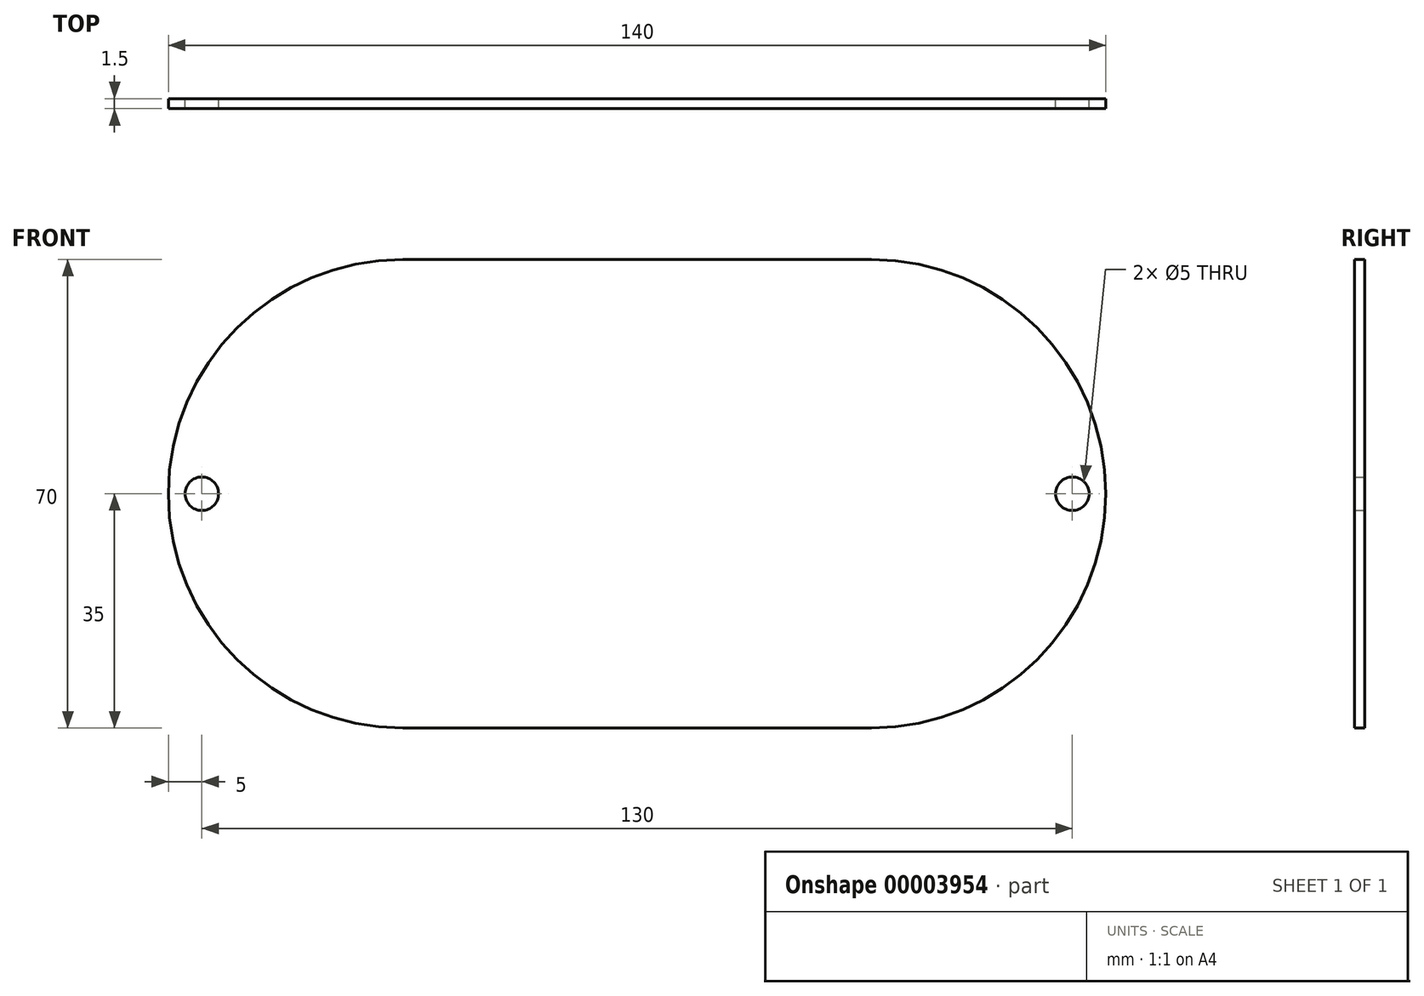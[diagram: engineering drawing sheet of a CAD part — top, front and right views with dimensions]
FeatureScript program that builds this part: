
annotation { "Feature Type Name" : "Feature", "Feature Type Description" : "" }
export const myFeature = defineFeature(function(context is Context, id is Id, definition is map)
    precondition{}
    {
        {
            var Q0;
            Q0=qCreatedBy(makeId("Front.planeOp"),FACE);
            var sketch = newSketch(context, id + "F0", { "sketchPlane" : qUnion([Q0])});
            skArc(sketch, "E0", {"start": v(-35, 35) * mm, "mid": v(-70, 0) * mm, "end": v(-35, -35) * mm});
            skLineSegment(sketch, "E1", {"start": v(-35, 35) * mm, "end": v(0, 35) * mm});
            skLineSegment(sketch, "E2", {"start": v(-35, -35) * mm, "end": v(0, -35) * mm});
            skLineSegment(sketch, "E3", {"start": v(0, -35) * mm, "end": v(0, 35) * mm});
            skCircle(sketch, "E4", {"center": v(-65, 0) * mm, "radius": 2.5 * mm});
            skLineSegment(sketch, "E5.0.MirrorCS", {"start": v(35, 35) * mm, "end": v(0, 35) * mm});
            skArc(sketch, "E6.0.MirrorCS", {"start": v(35, 35) * mm, "mid": v(70, 0) * mm, "end": v(35, -35) * mm});
            skCircle(sketch, "E7.0.MirrorC", {"center": v(65, 0) * mm, "radius": 2.5 * mm});
            skLineSegment(sketch, "E8.0.MirrorCS", {"start": v(35, -35) * mm, "end": v(0, -35) * mm});
            skSolve(sketch);
        }
        {
            var Q0;
            {var subQ0=makeQuery(id+"F0.imprint","IMPRINT",EDGE,{"derivedFrom":sQuery(id+"F0.wireOp",EDGE,"E3")});Q0=qUnion([makeQuery(id+"F0.imprint","IMPRINT",FACE,{"disambiguationData":[TD([[makeQuery(id+"F0.imprint","IMPRINT",EDGE,{"derivedFrom":sQuery(id+"F0.wireOp",EDGE,"E0")}),1.0]])]}),makeQuery(id+"F0.imprint","IMPRINT",FACE,{"disambiguationData":[TD([[subQ0,-1.0]])]})]);}
            extrude(context, id + "F1", {"entities" : qUnion([Q0]), "depth" : 1.5 * mm});
        }
    });
